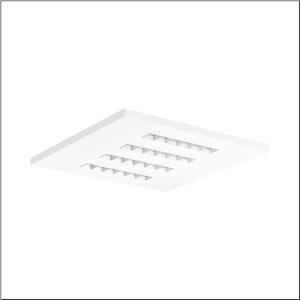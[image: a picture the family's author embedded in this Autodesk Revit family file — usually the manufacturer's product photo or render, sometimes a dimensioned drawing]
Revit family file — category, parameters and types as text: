
# Revit family: silica_r__21_square_51mx6mdu34w_1727
name_source: partatom
category: Lighting Fixtures
units: mm (PartAtom-declared; Revit-internal decimal feet)

## family parameters
Cut with Voids When Loaded = No
Host = Face
Light Source = No
Part Type = Normal
Room Calculation Point = No
Round Connector Dimension = Use Diameter
Shared = No

## types (1)
- --- (1 x LED, 4600 lm, 29.2 W, 3000K)
    Apparent Load = 29 VA
    CIE Flux Codes = 83 98 100 100 100
    Color Rendering = 80
    Color Temperature = 3000K
    Default Elevation = 1800 mm
    Description = Silica® 21 Square, office luminaire, primary light control with lens, of PMMA, primary anti-glare with reflector, of PC, white, CAT 2 (L<= 3000cd/m²), light emission: direct distribution, primary light characteristic: symmetric, installation type: lay-in mounting, LED, rated luminous flux: 4.600lm, luminous efficacy: 158lm/W, light colour: 830, colour temperature: 3000K, with terminal, 5-pole, mains connection: 220..240V, AC, 50/60Hz, rated input power: 29.2W, luminaire housing, of sheet steel, coated, traffic white (RAL 9016), module: M625, length: 622mm, width: 622mm, height: 33mm, protection rating (complete): IP20, insulation class (complete): insulation class I (protective earthing), certification: CE, permissible operating ambient temperature: -20..+40°C, standard: EN 50419, packaging unit: 1 piece
    Height = 0 mm  [stored 0 ft]
    Lamp = 1 x LED
    Lamp Light Flux = 4600 lm
    Lamp Power = 29.2 W
    Lamp count = 1
    Length = 622 mm
    Luminous efficacy = 158 lm/W
    Manufacturer = Siteco
    ModVariant = No
    Model = 51MX6MDU34W
    Mounting Place = Ceiling
    Mounting Type = Recessed
    Number of Poles = 1
    OnlyDefault = Yes
    Power Factor = 1
    Product Name = Silica® 21 Square
    Product group = office luminaire | ceiling recessed
    ProductGroupID = 401
    Protection Class = Protection class I
    Protection Degree = IP 20
    RLX_Detail_Level = 1
    RLX_Emergency_Light_Flux = 0 lm
    RLX_Emergency_Type = 0
    RLX_Emergency_Type_DB = No
    RlxData = <blob elided: 18493 chars, md5=07b2ac66>
    Socket = socket
    Standby Power = 0 W
    System Light Flux = 4600 lm
    System Power = 29 W
    Type Comments = factory setting: luminous flux: 100 % | dim-lin: 254 | 393 mA
    Type Image = l_1275220.jpg
    URL = http://relux.com
    VarID = @adj_036049
    Voltage = 0 V
    Weight = 0.00 kg
    Width = 622 mm

note: [stored X ft] marks values corroborated as IEEE doubles in the binary element streams (Revit-internal decimal feet)

## geometry (parser evidence)
native form markers: Blend x4, Sweep x12
no freeform markers — native parametric forms only
